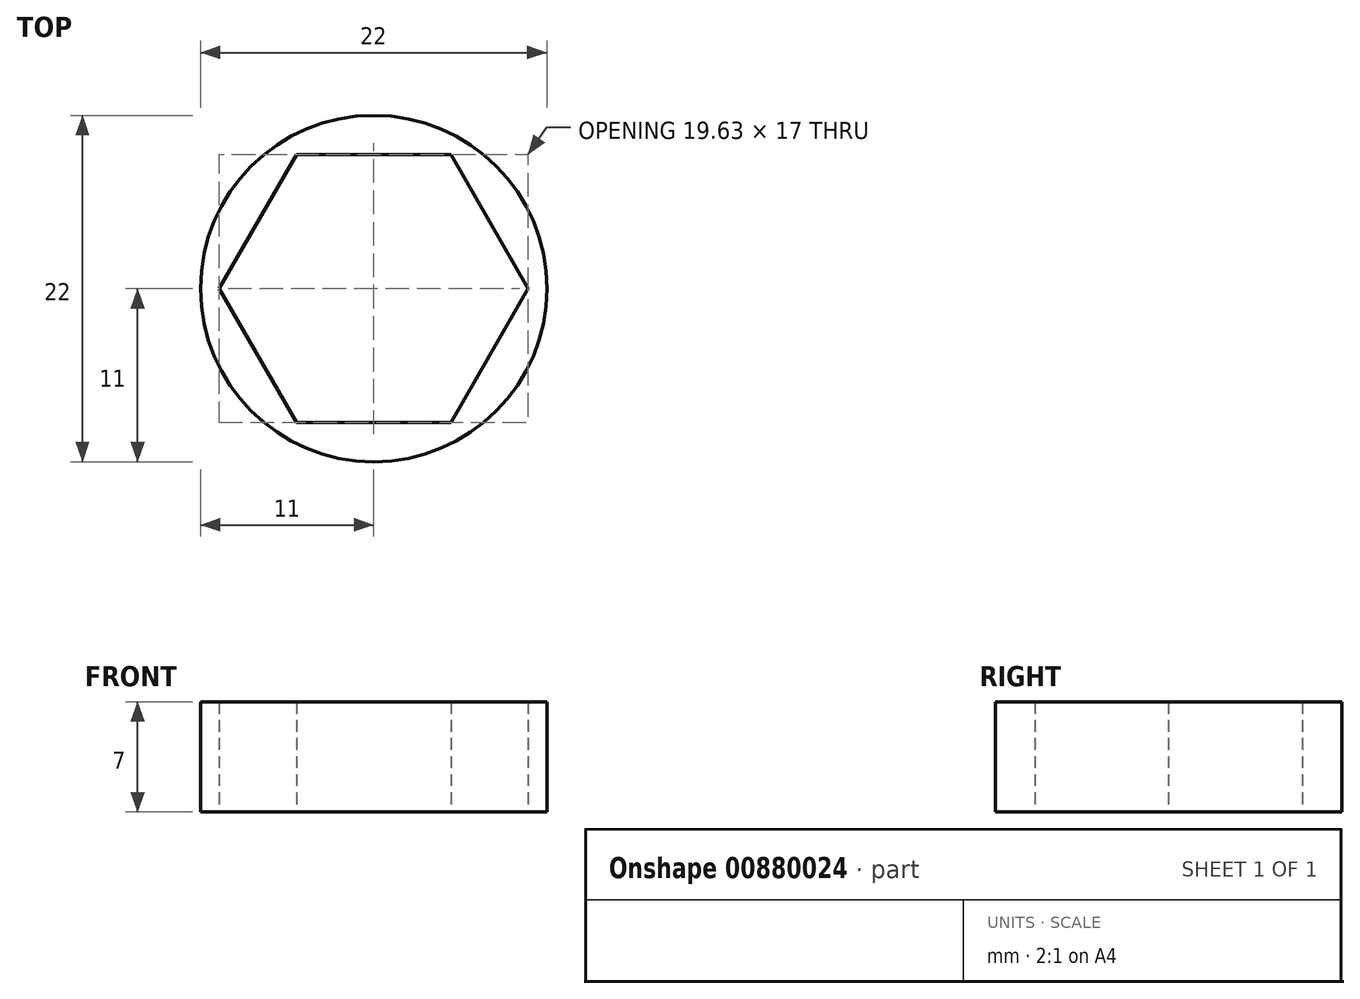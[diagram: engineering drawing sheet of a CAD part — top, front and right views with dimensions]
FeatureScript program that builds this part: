
annotation { "Feature Type Name" : "Feature", "Feature Type Description" : "" }
export const myFeature = defineFeature(function(context is Context, id is Id, definition is map)
    precondition{}
    {
        {
            var Q0;
            Q0=qCreatedBy(makeId("Top.planeOp"),FACE);
            var sketch = newSketch(context, id + "F0", { "sketchPlane" : qUnion([Q0])});
            skCircle(sketch, "E0", {"center": v(0, 0) * mm, "radius": 11 * mm});
            skCircle(sketch, "E1.cCircle", {"center": v(0, 0) * mm, "radius": 8.5 * mm, "construction": true});
            skLineSegment(sketch, "E1.0", {"start": v(4.9, -8.5) * mm, "end": v(-4.9, -8.5) * mm});
            skLineSegment(sketch, "E1.1", {"start": v(-4.9, -8.5) * mm, "end": v(-9.81, 0) * mm});
            skLineSegment(sketch, "E1.2", {"start": v(-9.81, 0) * mm, "end": v(-4.9, 8.5) * mm});
            skLineSegment(sketch, "E1.3", {"start": v(-4.9, 8.5) * mm, "end": v(4.9, 8.5) * mm});
            skLineSegment(sketch, "E1.4", {"start": v(4.9, 8.5) * mm, "end": v(9.81, 0) * mm});
            skLineSegment(sketch, "E1.5", {"start": v(9.81, 0) * mm, "end": v(4.9, -8.5) * mm});
            skPoint(sketch, "E1.0.midPoint", {"position": v(0, -8.5) * mm});
            skSolve(sketch);
        }
        {
            var Q0;
            Q0 = qSketchRegion(id + "F0", true);
            extrude(context, id + "F1", {"entities" : qUnion([Q0]), "depth" : 7 * mm, "offsetDistance" : 25 * mm});
        }
    });
